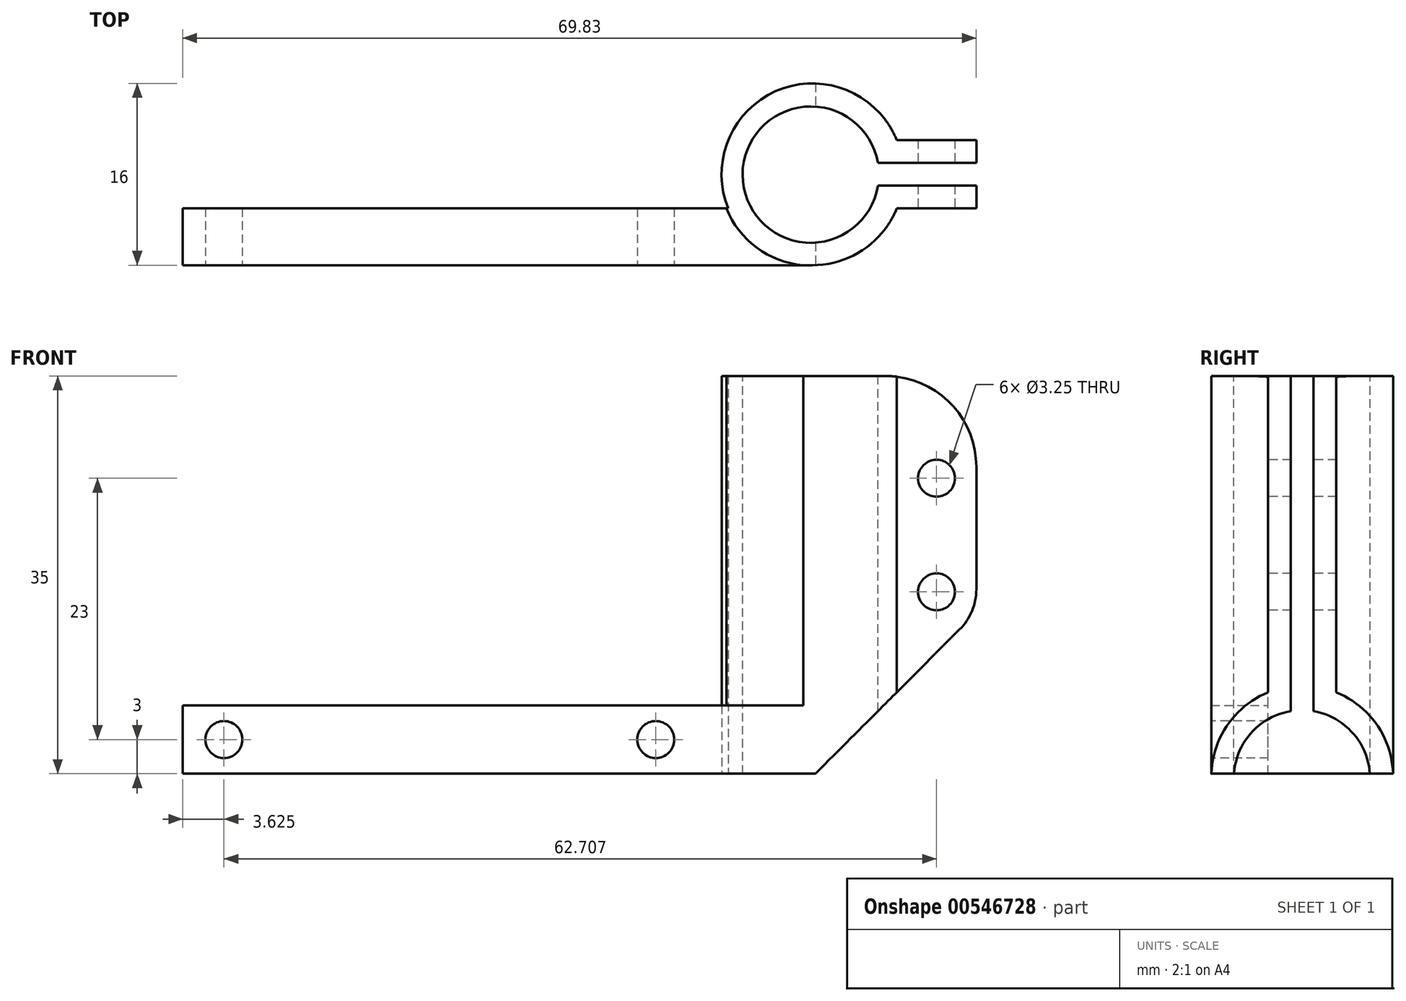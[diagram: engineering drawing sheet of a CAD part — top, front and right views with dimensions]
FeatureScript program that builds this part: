
annotation { "Feature Type Name" : "Feature", "Feature Type Description" : "" }
export const myFeature = defineFeature(function(context is Context, id is Id, definition is map)
    precondition{}
    {
        {
            var Q0;
            Q0=qCreatedBy(makeId("Top.planeOp"),FACE);
            var sketch = newSketch(context, id + "F0", { "sketchPlane" : qUnion([Q0])});
            skLineSegment(sketch, "E0.bottom", {"start": v(0, 0) * mm, "end": v(-48, 0) * mm});
            skLineSegment(sketch, "E0.top", {"start": v(0, 5) * mm, "end": v(-48, 5) * mm});
            skLineSegment(sketch, "E0.left", {"start": v(0, 0) * mm, "end": v(0, 5) * mm});
            skLineSegment(sketch, "E1", {"start": v(-48, 0) * mm, "end": v(-55.42, 0) * mm});
            skArc(sketch, "E2", {"start": v(-62.83, 5) * mm, "mid": v(-59.89, 1.37) * mm, "end": v(-55.42, 0) * mm});
            skLineSegment(sketch, "E3.bottom", {"start": v(-62.83, 11) * mm, "end": v(-69.83, 11) * mm});
            skLineSegment(sketch, "E3.top", {"start": v(-62.83, 5) * mm, "end": v(-69.83, 5) * mm});
            skLineSegment(sketch, "E3.right", {"start": v(-69.83, 11) * mm, "end": v(-69.83, 5) * mm});
            skArc(sketch, "E4.trimOffspring", {"start": v(-48, 5) * mm, "mid": v(-52.42, 15.42) * mm, "end": v(-62.83, 11) * mm});
            skSolve(sketch);
        }
        {
            var Q0;
            Q0 = qSketchRegion(id + "F0", true);
            extrude(context, id + "F1", {"entities" : qUnion([Q0]), "depth" : 35 * mm, "offsetDistance" : 25 * mm});
        }
        {
            var Q0;
            Q0=makeQuery(id+"F1.opExtrude","CAP_FACE",FACE,{"disambiguationData":[OSD([sQuery(id+"F0.wireOp",EDGE,"E0.bottom"),sQuery(id+"F0.wireOp",EDGE,"E0.top"),sQuery(id+"F0.wireOp",EDGE,"E0.left"),sQuery(id+"F0.wireOp",EDGE,"E1"),sQuery(id+"F0.wireOp",EDGE,"E2"),sQuery(id+"F0.wireOp",EDGE,"E3.bottom"),sQuery(id+"F0.wireOp",EDGE,"E3.top"),sQuery(id+"F0.wireOp",EDGE,"E3.right"),sQuery(id+"F0.wireOp",EDGE,"E4.trimOffspring")])],"isStart":false});
            cPlane(context, id + "F2", {"entities" : qUnion([Q0]), "cplaneType" : CPlaneType.OFFSET, "offset" : 0 * mm, "width" : 150 * mm, "height" : 150 * mm});
        }
        {
            var Q0;
            Q0=qCreatedBy(id+"F2.planeOp",FACE);
            var sketch = newSketch(context, id + "F3", { "sketchPlane" : qUnion([Q0])});
            skLineSegment(sketch, "E5.bottom", {"start": v(0, 0) * mm, "end": v(-56, 0) * mm});
            skLineSegment(sketch, "E5.top", {"start": v(0, 5) * mm, "end": v(-47.84, 5) * mm});
            skLineSegment(sketch, "E5.left", {"start": v(0, 0) * mm, "end": v(0, 5) * mm});
            skLineSegment(sketch, "E5.right", {"start": v(-56, 0) * mm, "end": v(-56, 0) * mm});
            skArc(sketch, "E6", {"start": v(-56, 0) * mm, "mid": v(-51.09, 1.15) * mm, "end": v(-47.84, 5) * mm});
            skSolve(sketch);
        }
        {
            var Q0;
            Q0 = qSketchRegion(id + "F3", true);
            extrude(context, id + "F4", {"entities" : qUnion([Q0]), "operationType" : NewBodyOperationType.REMOVE, "oppositeDirection" : true, "depth" : 29 * mm, "offsetDistance" : 25 * mm});
        }
        {
            var Q0;
            Q0=makeQuery(id+"F1.opExtrude","CAP_FACE",FACE,{"disambiguationData":[OSD([sQuery(id+"F0.wireOp",EDGE,"E0.bottom"),sQuery(id+"F0.wireOp",EDGE,"E0.top"),sQuery(id+"F0.wireOp",EDGE,"E0.left"),sQuery(id+"F0.wireOp",EDGE,"E1"),sQuery(id+"F0.wireOp",EDGE,"E2"),sQuery(id+"F0.wireOp",EDGE,"E3.bottom"),sQuery(id+"F0.wireOp",EDGE,"E3.top"),sQuery(id+"F0.wireOp",EDGE,"E3.right"),sQuery(id+"F0.wireOp",EDGE,"E4.trimOffspring")])],"isStart":false});
            var sketch = newSketch(context, id + "F5", { "sketchPlane" : qUnion([Q0])});
            skCircle(sketch, "E7", {"center": v(-55.26, 7.97) * mm, "radius": 6 * mm});
            skSolve(sketch);
        }
        {
            var Q0;
            Q0 = qSketchRegion(id + "F5", true);
            extrude(context, id + "F6", {"entities" : qUnion([Q0]), "operationType" : NewBodyOperationType.REMOVE, "oppositeDirection" : true, "depth" : 40 * mm, "offsetDistance" : 25 * mm});
        }
        {
            var Q0;
            Q0=qCreatedBy(id+"F2.planeOp",FACE);
            var sketch = newSketch(context, id + "F7", { "sketchPlane" : qUnion([Q0])});
            skLineSegment(sketch, "E8.bottom", {"start": v(-70.3, 9) * mm, "end": v(-58.02, 9) * mm});
            skLineSegment(sketch, "E8.top", {"start": v(-70.3, 7) * mm, "end": v(-58.02, 7) * mm});
            skLineSegment(sketch, "E8.left", {"start": v(-70.3, 9) * mm, "end": v(-70.3, 7) * mm});
            skLineSegment(sketch, "E8.right", {"start": v(-58.02, 9) * mm, "end": v(-58.02, 7) * mm});
            skSolve(sketch);
        }
        {
            var Q0;
            Q0 = qSketchRegion(id + "F7", true);
            extrude(context, id + "F8", {"entities" : qUnion([Q0]), "operationType" : NewBodyOperationType.REMOVE, "oppositeDirection" : true, "depth" : 40 * mm, "offsetDistance" : 25 * mm});
        }
        {
            var Q0;
            Q0=qCreatedBy(makeId("Front.planeOp"),FACE);
            var sketch = newSketch(context, id + "F9", { "sketchPlane" : qUnion([Q0])});
            skLineSegment(sketch, "E9", {"start": v(-55.68, 0) * mm, "end": v(-74.45, 0) * mm});
            skLineSegment(sketch, "E10", {"start": v(-74.45, 0) * mm, "end": v(-74.45, 18.78) * mm});
            skLineSegment(sketch, "E11", {"start": v(-74.45, 18.78) * mm, "end": v(-55.68, 0) * mm});
            skSolve(sketch);
        }
        {
            var Q0;
            Q0 = qSketchRegion(id + "F9", true);
            extrude(context, id + "F10", {"entities" : qUnion([Q0]), "operationType" : NewBodyOperationType.REMOVE, "oppositeDirection" : true, "depth" : 25 * mm, "offsetDistance" : 25 * mm});
        }
        {
            var Q0;
            {var subQ0=sQuery(id+"F0.wireOp",EDGE,"E3.right");var subQ1=sQuery(id+"F0.wireOp",EDGE,"E3.top");Q0=makeQuery(id+"F8.boolean.opBoolean","SPLIT",EDGE,{"disambiguationData":[TD([makeQuery(id+"F1.opExtrude","SWEPT_FACE",FACE,{"disambiguationData":[OSD([subQ1])]})])],"derivedFrom":makeQuery(id+"F1.opExtrude","CAP_EDGE",EDGE,{"disambiguationData":[OSD([subQ0])],"isStart":false})});}
            var Q1;
            {var subQ0=sQuery(id+"F0.wireOp",EDGE,"E3.right");var subQ1=sQuery(id+"F0.wireOp",EDGE,"E3.bottom");Q1=makeQuery(id+"F8.boolean.opBoolean","SPLIT",EDGE,{"disambiguationData":[TD([makeQuery(id+"F1.opExtrude","SWEPT_FACE",FACE,{"disambiguationData":[OSD([subQ1])]})])],"derivedFrom":makeQuery(id+"F1.opExtrude","CAP_EDGE",EDGE,{"disambiguationData":[OSD([subQ0])],"isStart":false})});}
            fillet(context, id + "F11", {"entities" : qUnion([Q0, Q1]), "radius" : 8 * mm, "tangentPropagation" : true, "allowEdgeOverflow" : false});
        }
        {
            var Q0;
            Q0=qCreatedBy(makeId("Front.planeOp"),FACE);
            var sketch = newSketch(context, id + "F12", { "sketchPlane" : qUnion([Q0])});
            skCircle(sketch, "E12", {"center": v(-3.62, 3) * mm, "radius": 1.63 * mm});
            skCircle(sketch, "E13", {"center": v(-41.62, 3) * mm, "radius": 1.63 * mm});
            skCircle(sketch, "E14", {"center": v(-66.33, 16) * mm, "radius": 1.63 * mm});
            skCircle(sketch, "E15", {"center": v(-66.33, 26) * mm, "radius": 1.63 * mm});
            skSolve(sketch);
        }
        {
            var Q0;
            Q0 = qSketchRegion(id + "F12", true);
            extrude(context, id + "F13", {"entities" : qUnion([Q0]), "operationType" : NewBodyOperationType.REMOVE, "oppositeDirection" : true, "depth" : 25 * mm, "offsetDistance" : 25 * mm});
        }
        {
            var Q0;
            Q0=makeQuery(id+"F1.opExtrude","SWEPT_BODY",BODY,{"disambiguationData":[OSD([sQuery(id+"F0.wireOp",EDGE,"E0.bottom"),sQuery(id+"F0.wireOp",EDGE,"E0.top"),sQuery(id+"F0.wireOp",EDGE,"E0.left"),sQuery(id+"F0.wireOp",EDGE,"E1"),sQuery(id+"F0.wireOp",EDGE,"E2"),sQuery(id+"F0.wireOp",EDGE,"E3.bottom"),sQuery(id+"F0.wireOp",EDGE,"E3.top"),sQuery(id+"F0.wireOp",EDGE,"E3.right"),sQuery(id+"F0.wireOp",EDGE,"E4.trimOffspring")])]});
            var Q1;
            Q1=qCreatedBy(makeId("Right.planeOp"),FACE);
            mirror(context, id + "F14", {"operationType" : NewBodyOperationType.ADD, "entities" : qUnion([Q0]), "mirrorPlane" : qUnion([Q1])});
        }
        {
            var Q0;
            Q0=qCreatedBy(makeId("Front.planeOp"),FACE);
            var sketch = newSketch(context, id + "F15", { "sketchPlane" : qUnion([Q0])});
            skLineSegment(sketch, "E16.bottom", {"start": v(0, 0) * mm, "end": v(-74.61, 0) * mm});
            skLineSegment(sketch, "E16.top", {"start": v(0, 42.97) * mm, "end": v(-74.61, 42.97) * mm});
            skLineSegment(sketch, "E16.left", {"start": v(0, 0) * mm, "end": v(0, 42.97) * mm});
            skLineSegment(sketch, "E16.right", {"start": v(-74.61, 0) * mm, "end": v(-74.61, 42.97) * mm});
            skSolve(sketch);
        }
        {
            var Q0;
            Q0 = qSketchRegion(id + "F15", true);
            extrude(context, id + "F16", {"entities" : qUnion([Q0]), "operationType" : NewBodyOperationType.REMOVE, "oppositeDirection" : true, "depth" : 25 * mm, "offsetDistance" : 25 * mm});
        }
        {
            var Q0;
            {var subQ1=sQuery(id+"F0.wireOp",EDGE,"E3.right");var subQ2=sQuery(id+"F0.wireOp",EDGE,"E3.top");Q0=makeQuery(id+"F14.opPattern","COPY",EDGE,{"derivedFrom":makeQuery(id+"F10.boolean.opBoolean","INTERSECT",EDGE,{"derivedFrom":[makeQuery(id+"F8.boolean.opBoolean","SPLIT",FACE,{"disambiguationData":[TD([makeQuery(id+"F1.opExtrude","SWEPT_FACE",FACE,{"disambiguationData":[OSD([subQ2])]})])],"derivedFrom":makeQuery(id+"F1.opExtrude","SWEPT_FACE",FACE,{"disambiguationData":[OSD([subQ1])]})}),makeQuery(id+"F10.opExtrude","SWEPT_FACE",FACE,{"disambiguationData":[OSD([sQuery(id+"F9.wireOp",EDGE,"E11")])]})]}),"instanceName":"1"});}
            var Q1;
            {var subQ1=sQuery(id+"F0.wireOp",EDGE,"E3.right");var subQ3=sQuery(id+"F0.wireOp",EDGE,"E3.bottom");Q1=makeQuery(id+"F14.opPattern","COPY",EDGE,{"derivedFrom":makeQuery(id+"F10.boolean.opBoolean","INTERSECT",EDGE,{"derivedFrom":[makeQuery(id+"F8.boolean.opBoolean","SPLIT",FACE,{"disambiguationData":[TD([makeQuery(id+"F1.opExtrude","SWEPT_FACE",FACE,{"disambiguationData":[OSD([subQ3])]})])],"derivedFrom":makeQuery(id+"F1.opExtrude","SWEPT_FACE",FACE,{"disambiguationData":[OSD([subQ1])]})}),makeQuery(id+"F10.opExtrude","SWEPT_FACE",FACE,{"disambiguationData":[OSD([sQuery(id+"F9.wireOp",EDGE,"E11")])]})]}),"instanceName":"1"});}
            fillet(context, id + "F17", {"entities" : qUnion([Q0, Q1]), "radius" : 5 * mm, "tangentPropagation" : true, "allowEdgeOverflow" : false});
        }
    });
